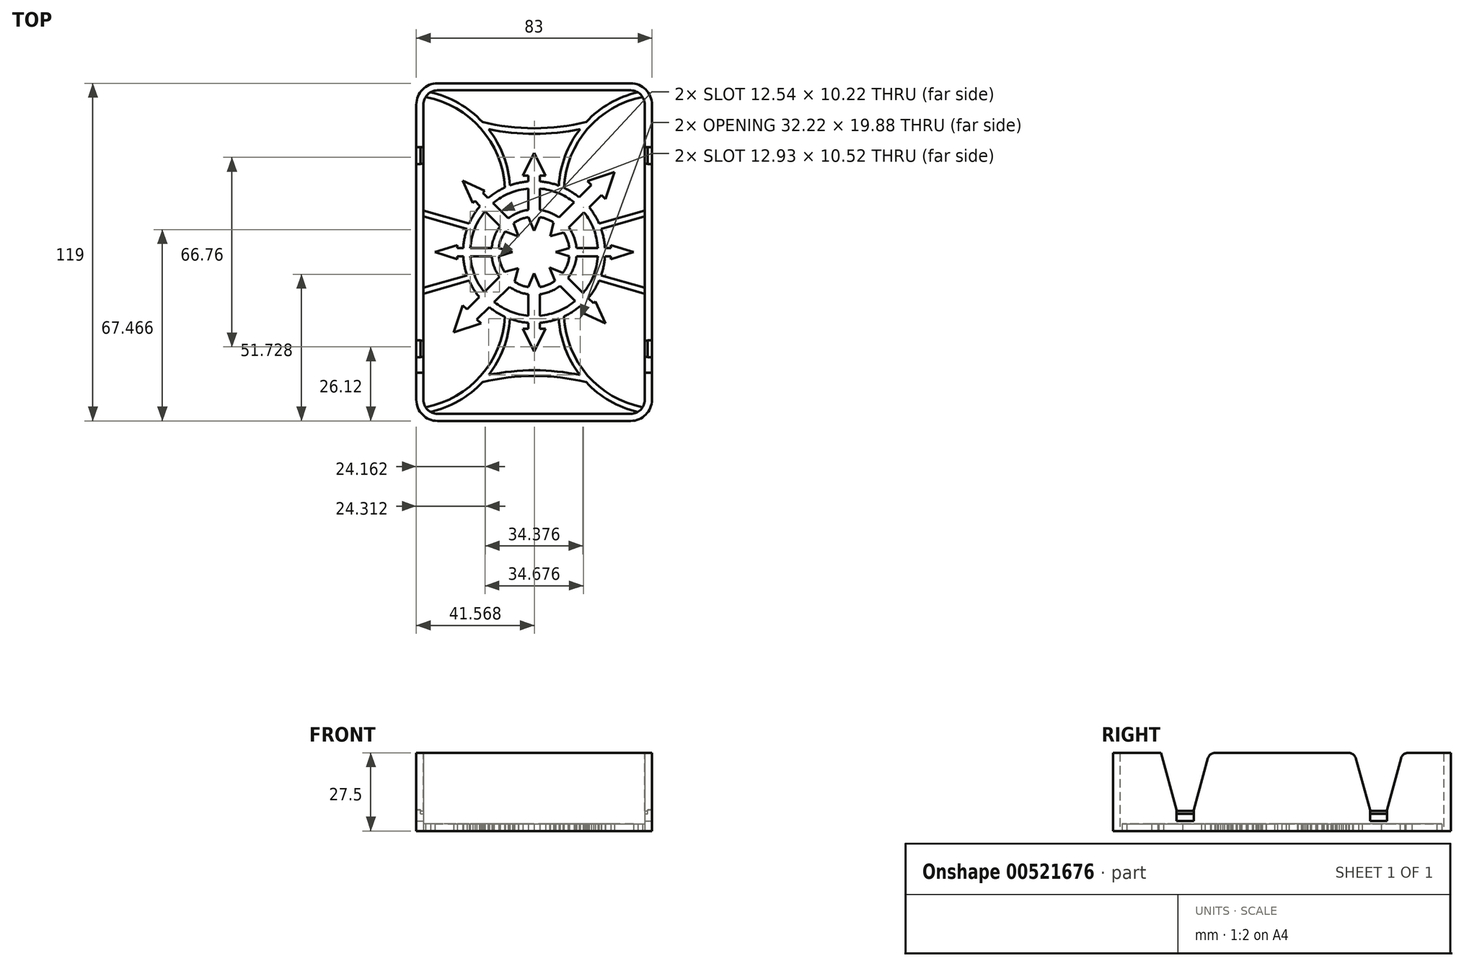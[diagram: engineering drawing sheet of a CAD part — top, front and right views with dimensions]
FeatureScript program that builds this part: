
annotation { "Feature Type Name" : "Feature", "Feature Type Description" : "" }
export const myFeature = defineFeature(function(context is Context, id is Id, definition is map)
    precondition{}
    {
        {
            var Q0;
            Q0=qCreatedBy(makeId("Top.planeOp"),FACE);
            var sketch = newSketch(context, id + "F0", { "sketchPlane" : qUnion([Q0])});
            skLineSegment(sketch, "E0.bottom", {"start": v(-34, 57) * mm, "end": v(34, 57) * mm});
            skLineSegment(sketch, "E0.top", {"start": v(-34, -57) * mm, "end": v(34, -57) * mm});
            skLineSegment(sketch, "E0.left", {"start": v(-39, 52) * mm, "end": v(-39, 14.68) * mm});
            skLineSegment(sketch, "E0.right", {"start": v(39, 52) * mm, "end": v(39, 14.68) * mm});
            skPoint(sketch, "E1.visualSharp", {"position": v(-39, 57) * mm});
            skArc(sketch, "E1.filletArc", {"start": v(-34, 57) * mm, "mid": v(-37.54, 55.54) * mm, "end": v(-39, 52) * mm});
            skPoint(sketch, "E2.visualSharp", {"position": v(39, 57) * mm});
            skArc(sketch, "E2.filletArc", {"start": v(39, 52) * mm, "mid": v(37.54, 55.54) * mm, "end": v(34, 57) * mm});
            skPoint(sketch, "E3.visualSharp", {"position": v(-39, -57) * mm});
            skArc(sketch, "E3.filletArc", {"start": v(-39, -52) * mm, "mid": v(-37.54, -55.54) * mm, "end": v(-34, -57) * mm});
            skPoint(sketch, "E4.visualSharp", {"position": v(39, -57) * mm});
            skArc(sketch, "E4.filletArc", {"start": v(34, -57) * mm, "mid": v(37.54, -55.54) * mm, "end": v(39, -52) * mm});
            skArc(sketch, "E5", {"start": v(-6.9, -10.43) * mm, "mid": v(-4.55, -11.64) * mm, "end": v(-2, -12.34) * mm});
            skArc(sketch, "E6.0", {"start": v(-8.7, -12.23) * mm, "mid": v(-5.5, -13.95) * mm, "end": v(-2, -14.87) * mm});
            skArc(sketch, "E7.0", {"start": v(-14.04, -17.58) * mm, "mid": v(-8.38, -20.88) * mm, "end": v(-2, -22.41) * mm});
            skArc(sketch, "E8.0", {"start": v(-15.82, -19.36) * mm, "mid": v(-13.18, -21.24) * mm, "end": v(-10.31, -22.77) * mm});
            skLineSegment(sketch, "E9", {"start": v(-20.15, -23.69) * mm, "end": v(-18.74, -25.1) * mm});
            skLineSegment(sketch, "E10", {"start": v(-23.69, -20.15) * mm, "end": v(-25.1, -18.74) * mm});
            skLineSegment(sketch, "E11", {"start": v(-28.28, -28.28) * mm, "end": v(-25.1, -18.74) * mm});
            skLineSegment(sketch, "E12", {"start": v(-28.28, -28.28) * mm, "end": v(-18.74, -25.1) * mm});
            skLineSegment(sketch, "E13.trimOffspring", {"start": v(-19.36, -15.82) * mm, "end": v(-23.69, -20.15) * mm});
            skLineSegment(sketch, "E14.trimOffspring", {"start": v(-15.82, -19.36) * mm, "end": v(-20.15, -23.69) * mm});
            skLineSegment(sketch, "E15", {"start": v(-6.9, -10.43) * mm, "end": v(-5.66, -5.66) * mm});
            skLineSegment(sketch, "E16", {"start": v(-5.66, -5.66) * mm, "end": v(-10.43, -6.9) * mm});
            skLineSegment(sketch, "E17.trimOffspring", {"start": v(-12.23, -8.7) * mm, "end": v(-17.58, -14.04) * mm});
            skLineSegment(sketch, "E18.trimOffspring", {"start": v(-8.7, -12.23) * mm, "end": v(-14.04, -17.58) * mm});
            skLineSegment(sketch, "E19.0", {"start": v(18.06, -20.89) * mm, "end": v(17.35, -21.6) * mm});
            skLineSegment(sketch, "E20.MirrorCS", {"start": v(20.89, -18.06) * mm, "end": v(21.6, -17.35) * mm});
            skLineSegment(sketch, "E21", {"start": v(25.13, -25.13) * mm, "end": v(17.35, -21.6) * mm});
            skLineSegment(sketch, "E22", {"start": v(25.13, -25.13) * mm, "end": v(21.6, -17.35) * mm});
            skArc(sketch, "E23.trimOffspring", {"start": v(19.04, -16.2) * mm, "mid": v(21.2, -13.26) * mm, "end": v(22.9, -10.03) * mm});
            skArc(sketch, "E24.trimOffspring", {"start": v(17.26, -14.43) * mm, "mid": v(20.88, -8.38) * mm, "end": v(22.45, -1.5) * mm});
            skLineSegment(sketch, "E25", {"start": v(7.31, -10.14) * mm, "end": v(5.47, -5.47) * mm});
            skLineSegment(sketch, "E26", {"start": v(5.47, -5.47) * mm, "end": v(10.14, -7.31) * mm});
            skArc(sketch, "E27.trimOffspring", {"start": v(11.93, -9.1) * mm, "mid": v(13.95, -5.5) * mm, "end": v(14.92, -1.5) * mm});
            skLineSegment(sketch, "E28.trimOffspring", {"start": v(19.04, -16.2) * mm, "end": v(20.89, -18.06) * mm});
            skLineSegment(sketch, "E29.trimOffspring", {"start": v(16.2, -19.04) * mm, "end": v(18.06, -20.89) * mm});
            skArc(sketch, "E30.trimOffspring", {"start": v(10.14, -7.31) * mm, "mid": v(11.64, -4.55) * mm, "end": v(12.4, -1.5) * mm});
            skLineSegment(sketch, "E31.trimOffspring", {"start": v(9.1, -11.93) * mm, "end": v(14.43, -17.26) * mm});
            skLineSegment(sketch, "E32.trimOffspring", {"start": v(11.93, -9.1) * mm, "end": v(17.26, -14.43) * mm});
            skLineSegment(sketch, "E33.MirrorCS", {"start": v(-11.93, 9.1) * mm, "end": v(-17.26, 14.43) * mm});
            skLineSegment(sketch, "E34.MirrorCS", {"start": v(-9.1, 11.93) * mm, "end": v(-14.43, 17.26) * mm});
            skLineSegment(sketch, "E35.MirrorCS", {"start": v(-5.47, 5.47) * mm, "end": v(-7.31, 10.14) * mm});
            skLineSegment(sketch, "E36.MirrorCS", {"start": v(-10.14, 7.31) * mm, "end": v(-5.47, 5.47) * mm});
            skLineSegment(sketch, "E37.MirrorCS", {"start": v(-16.2, 19.04) * mm, "end": v(-18.06, 20.89) * mm});
            skLineSegment(sketch, "E38.MirrorCS", {"start": v(-19.04, 16.2) * mm, "end": v(-20.89, 18.06) * mm});
            skLineSegment(sketch, "E39.MirrorCS", {"start": v(-20.89, 18.06) * mm, "end": v(-21.6, 17.35) * mm});
            skLineSegment(sketch, "E40.MirrorCS", {"start": v(-25.13, 25.13) * mm, "end": v(-21.6, 17.35) * mm});
            skLineSegment(sketch, "E41.MirrorCS", {"start": v(-25.13, 25.13) * mm, "end": v(-17.35, 21.6) * mm});
            skLineSegment(sketch, "E42.MirrorCS", {"start": v(-18.06, 20.89) * mm, "end": v(-17.35, 21.6) * mm});
            skArc(sketch, "E43.trimOffspring", {"start": v(-19.04, 16.2) * mm, "mid": v(-21.2, 13.26) * mm, "end": v(-22.9, 10.03) * mm});
            skArc(sketch, "E44.trimOffspring", {"start": v(-17.26, 14.43) * mm, "mid": v(-20.88, 8.38) * mm, "end": v(-22.45, 1.5) * mm});
            skArc(sketch, "E45.trimOffspring", {"start": v(-11.93, 9.1) * mm, "mid": v(-13.95, 5.5) * mm, "end": v(-14.92, 1.5) * mm});
            skArc(sketch, "E46.trimOffspring", {"start": v(-10.14, 7.31) * mm, "mid": v(-11.64, 4.55) * mm, "end": v(-12.4, 1.5) * mm});
            skLineSegment(sketch, "E47.0", {"start": v(-2, -27) * mm, "end": v(-4, -27) * mm});
            skLineSegment(sketch, "E48", {"start": v(0, -35) * mm, "end": v(-4, -27) * mm});
            skLineSegment(sketch, "E49.MirrorCS", {"start": v(2, -27) * mm, "end": v(4, -27) * mm});
            skLineSegment(sketch, "E50.MirrorCS", {"start": v(0, -35) * mm, "end": v(4, -27) * mm});
            skLineSegment(sketch, "E51", {"start": v(-2, -12.34) * mm, "end": v(0, -7.51) * mm});
            skLineSegment(sketch, "E52", {"start": v(0, -7.51) * mm, "end": v(2, -12.34) * mm});
            skArc(sketch, "E53.trimOffspring", {"start": v(2, -12.34) * mm, "mid": v(4.78, -11.55) * mm, "end": v(7.31, -10.14) * mm});
            skArc(sketch, "E54.trimOffspring", {"start": v(2, -14.87) * mm, "mid": v(5.74, -13.86) * mm, "end": v(9.1, -11.93) * mm});
            skArc(sketch, "E55.trimOffspring", {"start": v(2, -22.41) * mm, "mid": v(8.61, -20.79) * mm, "end": v(14.43, -17.26) * mm});
            skArc(sketch, "E56.trimOffspring", {"start": v(2, -24.92) * mm, "mid": v(5.4, -24.41) * mm, "end": v(8.7, -23.44) * mm});
            skLineSegment(sketch, "E57.trimOffspring", {"start": v(-2, -24.92) * mm, "end": v(-2, -27) * mm});
            skLineSegment(sketch, "E58.trimOffspring", {"start": v(2, -24.92) * mm, "end": v(2, -27) * mm});
            skLineSegment(sketch, "E59.trimOffspring", {"start": v(2, -14.87) * mm, "end": v(2, -22.41) * mm});
            skLineSegment(sketch, "E60.trimOffspring", {"start": v(-2, -14.87) * mm, "end": v(-2, -22.41) * mm});
            skLineSegment(sketch, "E61.MirrorCS", {"start": v(-2, 12.34) * mm, "end": v(0, 7.51) * mm});
            skLineSegment(sketch, "E62.MirrorCS", {"start": v(0, 7.51) * mm, "end": v(2, 12.34) * mm});
            skLineSegment(sketch, "E63.MirrorCS", {"start": v(-2, 14.87) * mm, "end": v(-2, 22.41) * mm});
            skLineSegment(sketch, "E64.MirrorCS", {"start": v(2, 14.87) * mm, "end": v(2, 22.41) * mm});
            skLineSegment(sketch, "E65.MirrorCS", {"start": v(0, 35) * mm, "end": v(-4, 27) * mm});
            skLineSegment(sketch, "E66.MirrorCS", {"start": v(0, 35) * mm, "end": v(4, 27) * mm});
            skLineSegment(sketch, "E67.MirrorCS", {"start": v(2, 27) * mm, "end": v(4, 27) * mm});
            skLineSegment(sketch, "E68.MirrorCS", {"start": v(2, 24.92) * mm, "end": v(2, 27) * mm});
            skLineSegment(sketch, "E69.MirrorCS", {"start": v(-2, 24.92) * mm, "end": v(-2, 27) * mm});
            skLineSegment(sketch, "E70.MirrorCS", {"start": v(-2, 27) * mm, "end": v(-4, 27) * mm});
            skArc(sketch, "E71.trimOffspring", {"start": v(-2, 24.92) * mm, "mid": v(-5.32, 24.43) * mm, "end": v(-8.54, 23.5) * mm});
            skArc(sketch, "E72.trimOffspring", {"start": v(-2, 22.41) * mm, "mid": v(-8.61, 20.79) * mm, "end": v(-14.43, 17.26) * mm});
            skArc(sketch, "E73.trimOffspring", {"start": v(-2, 14.87) * mm, "mid": v(-5.74, 13.86) * mm, "end": v(-9.1, 11.93) * mm});
            skArc(sketch, "E74.trimOffspring", {"start": v(-2, 12.34) * mm, "mid": v(-4.78, 11.55) * mm, "end": v(-7.31, 10.14) * mm});
            skLineSegment(sketch, "E75.MirrorCS", {"start": v(5.66, 5.66) * mm, "end": v(6.9, 10.43) * mm});
            skLineSegment(sketch, "E76.MirrorCS", {"start": v(10.43, 6.9) * mm, "end": v(5.66, 5.66) * mm});
            skLineSegment(sketch, "E77.MirrorCS", {"start": v(8.7, 12.23) * mm, "end": v(14.04, 17.58) * mm});
            skLineSegment(sketch, "E78.MirrorCS", {"start": v(12.23, 8.7) * mm, "end": v(17.58, 14.04) * mm});
            skLineSegment(sketch, "E79.MirrorCS", {"start": v(19.36, 15.82) * mm, "end": v(23.69, 20.15) * mm});
            skLineSegment(sketch, "E80.MirrorCS", {"start": v(23.69, 20.15) * mm, "end": v(25.1, 18.74) * mm});
            skLineSegment(sketch, "E81.MirrorCS", {"start": v(28.28, 28.28) * mm, "end": v(25.1, 18.74) * mm});
            skLineSegment(sketch, "E82.MirrorCS", {"start": v(28.28, 28.28) * mm, "end": v(18.74, 25.1) * mm});
            skLineSegment(sketch, "E83.MirrorCS", {"start": v(20.15, 23.69) * mm, "end": v(18.74, 25.1) * mm});
            skLineSegment(sketch, "E84.MirrorCS", {"start": v(15.82, 19.36) * mm, "end": v(20.15, 23.69) * mm});
            skArc(sketch, "E85.trimOffspring", {"start": v(6.9, 10.43) * mm, "mid": v(4.55, 11.64) * mm, "end": v(2, 12.34) * mm});
            skArc(sketch, "E86.trimOffspring", {"start": v(8.7, 12.23) * mm, "mid": v(5.5, 13.95) * mm, "end": v(2, 14.87) * mm});
            skArc(sketch, "E87.trimOffspring", {"start": v(14.04, 17.58) * mm, "mid": v(8.38, 20.88) * mm, "end": v(2, 22.41) * mm});
            skArc(sketch, "E88.trimOffspring", {"start": v(15.82, 19.36) * mm, "mid": v(13.29, 21.18) * mm, "end": v(10.55, 22.67) * mm});
            skLineSegment(sketch, "E89.0", {"start": v(-14.92, 1.5) * mm, "end": v(-22.45, 1.5) * mm});
            skLineSegment(sketch, "E90.0", {"start": v(-14.92, -1.5) * mm, "end": v(-22.45, -1.5) * mm});
            skLineSegment(sketch, "E91.0", {"start": v(-27, 1.5) * mm, "end": v(-27, 2.5) * mm});
            skLineSegment(sketch, "E92", {"start": v(-35, 0) * mm, "end": v(-27, 2.5) * mm});
            skLineSegment(sketch, "E93.MirrorCS", {"start": v(-35, 0) * mm, "end": v(-27, -2.5) * mm});
            skLineSegment(sketch, "E94.MirrorCS", {"start": v(-27, -1.5) * mm, "end": v(-27, -2.5) * mm});
            skLineSegment(sketch, "E95", {"start": v(-12.4, 1.5) * mm, "end": v(-7.65, 0) * mm});
            skLineSegment(sketch, "E96", {"start": v(-7.65, 0) * mm, "end": v(-12.4, -1.5) * mm});
            skArc(sketch, "E97.trimOffspring", {"start": v(-24.95, -1.5) * mm, "mid": v(-24.52, -4.88) * mm, "end": v(-23.63, -8.16) * mm});
            skArc(sketch, "E98.trimOffspring", {"start": v(-12.4, -1.5) * mm, "mid": v(-11.73, -4.31) * mm, "end": v(-10.43, -6.9) * mm});
            skArc(sketch, "E99.trimOffspring", {"start": v(-14.92, -1.5) * mm, "mid": v(-14.04, -5.27) * mm, "end": v(-12.23, -8.7) * mm});
            skArc(sketch, "E100.trimOffspring", {"start": v(-22.45, -1.5) * mm, "mid": v(-20.97, -8.14) * mm, "end": v(-17.58, -14.04) * mm});
            skLineSegment(sketch, "E101.MirrorCS", {"start": v(7.65, 0) * mm, "end": v(12.4, -1.5) * mm});
            skLineSegment(sketch, "E102.MirrorCS", {"start": v(12.4, 1.5) * mm, "end": v(7.65, 0) * mm});
            skLineSegment(sketch, "E103.MirrorCS", {"start": v(14.92, 1.5) * mm, "end": v(22.45, 1.5) * mm});
            skLineSegment(sketch, "E104.MirrorCS", {"start": v(14.92, -1.5) * mm, "end": v(22.45, -1.5) * mm});
            skLineSegment(sketch, "E105.MirrorCS", {"start": v(27, 1.5) * mm, "end": v(27, 2.5) * mm});
            skLineSegment(sketch, "E106.MirrorCS", {"start": v(27, -1.5) * mm, "end": v(27, -2.5) * mm});
            skLineSegment(sketch, "E107.MirrorCS", {"start": v(35, 0) * mm, "end": v(27, -2.5) * mm});
            skLineSegment(sketch, "E108.MirrorCS", {"start": v(35, 0) * mm, "end": v(27, 2.5) * mm});
            skLineSegment(sketch, "E109.trimOffspring", {"start": v(-24.95, 1.5) * mm, "end": v(-27, 1.5) * mm});
            skLineSegment(sketch, "E110.trimOffspring", {"start": v(-24.95, -1.5) * mm, "end": v(-27, -1.5) * mm});
            skArc(sketch, "E111.trimOffspring", {"start": v(12.4, 1.5) * mm, "mid": v(11.73, 4.31) * mm, "end": v(10.43, 6.9) * mm});
            skArc(sketch, "E112.trimOffspring", {"start": v(14.92, 1.5) * mm, "mid": v(14.04, 5.27) * mm, "end": v(12.23, 8.7) * mm});
            skArc(sketch, "E113.trimOffspring", {"start": v(22.45, 1.5) * mm, "mid": v(20.97, 8.14) * mm, "end": v(17.58, 14.04) * mm});
            skArc(sketch, "E114.trimOffspring", {"start": v(24.95, 1.5) * mm, "mid": v(24.52, 4.88) * mm, "end": v(23.63, 8.16) * mm});
            skLineSegment(sketch, "E115.trimOffspring", {"start": v(24.95, 1.5) * mm, "end": v(27, 1.5) * mm});
            skLineSegment(sketch, "E116.trimOffspring", {"start": v(24.95, -1.5) * mm, "end": v(27, -1.5) * mm});
            skArc(sketch, "E117.0", {"start": v(-34, 59.5) * mm, "mid": v(-39.3, 57.3) * mm, "end": v(-41.5, 52) * mm});
            skLineSegment(sketch, "E117.1", {"start": v(-41.5, 52) * mm, "end": v(-41.5, -52) * mm});
            skLineSegment(sketch, "E117.2", {"start": v(-34, 59.5) * mm, "end": v(34, 59.5) * mm});
            skArc(sketch, "E117.3", {"start": v(-41.5, -52) * mm, "mid": v(-39.3, -57.3) * mm, "end": v(-34, -59.5) * mm});
            skArc(sketch, "E117.4", {"start": v(41.5, 52) * mm, "mid": v(39.3, 57.3) * mm, "end": v(34, 59.5) * mm});
            skLineSegment(sketch, "E117.5", {"start": v(41.5, 52) * mm, "end": v(41.5, -52) * mm});
            skArc(sketch, "E117.6", {"start": v(34, -59.5) * mm, "mid": v(39.3, -57.3) * mm, "end": v(41.5, -52) * mm});
            skLineSegment(sketch, "E117.7", {"start": v(-34, -59.5) * mm, "end": v(34, -59.5) * mm});
            skArc(sketch, "E118.0", {"start": v(-36.5, -56.33) * mm, "mid": v(-26.57, -52.47) * mm, "end": v(-18.22, -45.86) * mm});
            skArc(sketch, "E119.0", {"start": v(-38.24, -54.65) * mm, "mid": v(-18.75, -43.55) * mm, "end": v(-10.31, -22.77) * mm});
            skArc(sketch, "E120.0", {"start": v(8.7, -23.44) * mm, "mid": v(10.94, -33.94) * mm, "end": v(16.18, -43.32) * mm});
            skArc(sketch, "E121.0", {"start": v(10.55, -22.67) * mm, "mid": v(18.84, -43.47) * mm, "end": v(38.24, -54.66) * mm});
            skArc(sketch, "E122.MirrorCS", {"start": v(-36.5, 56.33) * mm, "mid": v(-26.57, 52.47) * mm, "end": v(-18.22, 45.86) * mm});
            skArc(sketch, "E123.MirrorCS", {"start": v(-38.24, 54.65) * mm, "mid": v(-18.75, 43.55) * mm, "end": v(-10.31, 22.77) * mm});
            skArc(sketch, "E124.MirrorCS", {"start": v(10.55, 22.67) * mm, "mid": v(18.84, 43.47) * mm, "end": v(38.24, 54.66) * mm});
            skArc(sketch, "E125.MirrorCS", {"start": v(8.7, 23.44) * mm, "mid": v(10.94, 33.94) * mm, "end": v(16.18, 43.32) * mm});
            skArc(sketch, "E126.0", {"start": v(16.18, -43.32) * mm, "mid": v(0.07, -41.65) * mm, "end": v(-16.04, -43.32) * mm});
            skArc(sketch, "E127.0", {"start": v(18.35, -45.86) * mm, "mid": v(0.06, -43.65) * mm, "end": v(-18.22, -45.86) * mm});
            skArc(sketch, "E128.MirrorCS", {"start": v(16.18, 43.32) * mm, "mid": v(0.07, 41.65) * mm, "end": v(-16.04, 43.32) * mm});
            skArc(sketch, "E129.MirrorCS", {"start": v(18.35, 45.86) * mm, "mid": v(0.06, 43.65) * mm, "end": v(-18.22, 45.86) * mm});
            skArc(sketch, "E130.trimOffspring", {"start": v(-16.04, -43.32) * mm, "mid": v(-10.8, -33.97) * mm, "end": v(-8.54, -23.5) * mm});
            skArc(sketch, "E131.trimOffspring", {"start": v(18.35, -45.86) * mm, "mid": v(26.64, -52.45) * mm, "end": v(36.5, -56.33) * mm});
            skArc(sketch, "E132.trimOffspring", {"start": v(10.55, -22.67) * mm, "mid": v(13.5, -21.04) * mm, "end": v(16.2, -19.04) * mm});
            skArc(sketch, "E133.trimOffspring", {"start": v(-8.54, -23.5) * mm, "mid": v(-5.32, -24.43) * mm, "end": v(-2, -24.92) * mm});
            skArc(sketch, "E134.trimOffspring", {"start": v(-10.31, 22.77) * mm, "mid": v(-13.4, 21.11) * mm, "end": v(-16.2, 19.04) * mm});
            skArc(sketch, "E135.trimOffspring", {"start": v(8.7, 23.44) * mm, "mid": v(5.4, 24.41) * mm, "end": v(2, 24.92) * mm});
            skArc(sketch, "E136.trimOffspring", {"start": v(18.35, 45.86) * mm, "mid": v(26.64, 52.45) * mm, "end": v(36.5, 56.33) * mm});
            skArc(sketch, "E137.trimOffspring", {"start": v(-16.04, 43.32) * mm, "mid": v(-10.8, 33.97) * mm, "end": v(-8.54, 23.5) * mm});
            skLineSegment(sketch, "E138.0", {"start": v(-23.63, -8.16) * mm, "end": v(-39, -12.6) * mm});
            skLineSegment(sketch, "E139.0", {"start": v(-22.9, -10.03) * mm, "end": v(-39, -14.68) * mm});
            skLineSegment(sketch, "E140.trimOffspring", {"start": v(-39, -14.68) * mm, "end": v(-39, -52) * mm});
            skArc(sketch, "E141.trimOffspring", {"start": v(-22.9, -10.03) * mm, "mid": v(-21.33, -13.05) * mm, "end": v(-19.36, -15.82) * mm});
            skLineSegment(sketch, "E142.MirrorCS", {"start": v(-23.63, 8.16) * mm, "end": v(-39, 12.6) * mm});
            skLineSegment(sketch, "E143.MirrorCS", {"start": v(-22.9, 10.03) * mm, "end": v(-39, 14.68) * mm});
            skLineSegment(sketch, "E144.MirrorCS", {"start": v(23.63, -8.16) * mm, "end": v(39, -12.6) * mm});
            skLineSegment(sketch, "E145.MirrorCS", {"start": v(22.9, -10.03) * mm, "end": v(39, -14.68) * mm});
            skLineSegment(sketch, "E146.MirrorCS", {"start": v(23.63, 8.16) * mm, "end": v(39, 12.6) * mm});
            skLineSegment(sketch, "E147.MirrorCS", {"start": v(22.9, 10.03) * mm, "end": v(39, 14.68) * mm});
            skLineSegment(sketch, "E148.trimOffspring", {"start": v(-39, 12.6) * mm, "end": v(-39, -12.6) * mm});
            skArc(sketch, "E149.trimOffspring", {"start": v(-23.63, 8.16) * mm, "mid": v(-24.52, 4.88) * mm, "end": v(-24.95, 1.5) * mm});
            skArc(sketch, "E150.trimOffspring", {"start": v(22.9, 10.03) * mm, "mid": v(21.33, 13.05) * mm, "end": v(19.36, 15.82) * mm});
            skLineSegment(sketch, "E151.trimOffspring", {"start": v(39, 12.6) * mm, "end": v(39, -12.6) * mm});
            skArc(sketch, "E152.trimOffspring", {"start": v(23.63, -8.16) * mm, "mid": v(24.52, -4.88) * mm, "end": v(24.95, -1.5) * mm});
            skLineSegment(sketch, "E153.trimOffspring", {"start": v(39, -14.68) * mm, "end": v(39, -52) * mm});
            skSolve(sketch);
        }
        {
            var Q0;
            Q0 = qSketchRegion(id + "F0", true);
            extrude(context, id + "F1", {"entities" : qUnion([Q0]), "depth" : 2.5 * mm, "offsetDistance" : 25 * mm});
        }
        {
            var Q0;
            Q0=makeQuery(id+"F1.opExtrude","CAP_FACE",FACE,{"disambiguationData":[OSD([sQuery(id+"F0.wireOp",EDGE,"E0.bottom"),sQuery(id+"F0.wireOp",EDGE,"E0.top"),sQuery(id+"F0.wireOp",EDGE,"E0.left"),sQuery(id+"F0.wireOp",EDGE,"E0.right"),sQuery(id+"F0.wireOp",EDGE,"E1.filletArc"),sQuery(id+"F0.wireOp",EDGE,"E2.filletArc"),sQuery(id+"F0.wireOp",EDGE,"E3.filletArc"),sQuery(id+"F0.wireOp",EDGE,"E4.filletArc"),sQuery(id+"F0.wireOp",EDGE,"E5"),sQuery(id+"F0.wireOp",EDGE,"E6.0"),sQuery(id+"F0.wireOp",EDGE,"E7.0"),sQuery(id+"F0.wireOp",EDGE,"E8.0"),sQuery(id+"F0.wireOp",EDGE,"E9"),sQuery(id+"F0.wireOp",EDGE,"E10"),sQuery(id+"F0.wireOp",EDGE,"E11"),sQuery(id+"F0.wireOp",EDGE,"E12"),sQuery(id+"F0.wireOp",EDGE,"E13.trimOffspring"),sQuery(id+"F0.wireOp",EDGE,"E14.trimOffspring"),sQuery(id+"F0.wireOp",EDGE,"E15"),sQuery(id+"F0.wireOp",EDGE,"E16"),sQuery(id+"F0.wireOp",EDGE,"E17.trimOffspring"),sQuery(id+"F0.wireOp",EDGE,"E18.trimOffspring"),sQuery(id+"F0.wireOp",EDGE,"E19.0"),sQuery(id+"F0.wireOp",EDGE,"E20.MirrorCS"),sQuery(id+"F0.wireOp",EDGE,"E21"),sQuery(id+"F0.wireOp",EDGE,"E22"),sQuery(id+"F0.wireOp",EDGE,"E23.trimOffspring"),sQuery(id+"F0.wireOp",EDGE,"E24.trimOffspring"),sQuery(id+"F0.wireOp",EDGE,"E25"),sQuery(id+"F0.wireOp",EDGE,"E26"),sQuery(id+"F0.wireOp",EDGE,"E27.trimOffspring"),sQuery(id+"F0.wireOp",EDGE,"E28.trimOffspring"),sQuery(id+"F0.wireOp",EDGE,"E29.trimOffspring"),sQuery(id+"F0.wireOp",EDGE,"E30.trimOffspring"),sQuery(id+"F0.wireOp",EDGE,"E31.trimOffspring"),sQuery(id+"F0.wireOp",EDGE,"E32.trimOffspring"),sQuery(id+"F0.wireOp",EDGE,"E33.MirrorCS"),sQuery(id+"F0.wireOp",EDGE,"E34.MirrorCS"),sQuery(id+"F0.wireOp",EDGE,"E35.MirrorCS"),sQuery(id+"F0.wireOp",EDGE,"E36.MirrorCS"),sQuery(id+"F0.wireOp",EDGE,"E37.MirrorCS"),sQuery(id+"F0.wireOp",EDGE,"E38.MirrorCS"),sQuery(id+"F0.wireOp",EDGE,"E39.MirrorCS"),sQuery(id+"F0.wireOp",EDGE,"E40.MirrorCS"),sQuery(id+"F0.wireOp",EDGE,"E41.MirrorCS"),sQuery(id+"F0.wireOp",EDGE,"E42.MirrorCS"),sQuery(id+"F0.wireOp",EDGE,"E43.trimOffspring"),sQuery(id+"F0.wireOp",EDGE,"E44.trimOffspring"),sQuery(id+"F0.wireOp",EDGE,"E45.trimOffspring"),sQuery(id+"F0.wireOp",EDGE,"E46.trimOffspring"),sQuery(id+"F0.wireOp",EDGE,"E47.0"),sQuery(id+"F0.wireOp",EDGE,"E48"),sQuery(id+"F0.wireOp",EDGE,"E49.MirrorCS"),sQuery(id+"F0.wireOp",EDGE,"E50.MirrorCS"),sQuery(id+"F0.wireOp",EDGE,"E51"),sQuery(id+"F0.wireOp",EDGE,"E52"),sQuery(id+"F0.wireOp",EDGE,"E53.trimOffspring"),sQuery(id+"F0.wireOp",EDGE,"E54.trimOffspring"),sQuery(id+"F0.wireOp",EDGE,"E55.trimOffspring"),sQuery(id+"F0.wireOp",EDGE,"E56.trimOffspring"),sQuery(id+"F0.wireOp",EDGE,"E57.trimOffspring"),sQuery(id+"F0.wireOp",EDGE,"E58.trimOffspring"),sQuery(id+"F0.wireOp",EDGE,"E59.trimOffspring"),sQuery(id+"F0.wireOp",EDGE,"E60.trimOffspring"),sQuery(id+"F0.wireOp",EDGE,"E61.MirrorCS"),sQuery(id+"F0.wireOp",EDGE,"E62.MirrorCS"),sQuery(id+"F0.wireOp",EDGE,"E63.MirrorCS"),sQuery(id+"F0.wireOp",EDGE,"E64.MirrorCS"),sQuery(id+"F0.wireOp",EDGE,"E65.MirrorCS"),sQuery(id+"F0.wireOp",EDGE,"E66.MirrorCS"),sQuery(id+"F0.wireOp",EDGE,"E67.MirrorCS"),sQuery(id+"F0.wireOp",EDGE,"E68.MirrorCS"),sQuery(id+"F0.wireOp",EDGE,"E69.MirrorCS"),sQuery(id+"F0.wireOp",EDGE,"E70.MirrorCS"),sQuery(id+"F0.wireOp",EDGE,"E71.trimOffspring"),sQuery(id+"F0.wireOp",EDGE,"E72.trimOffspring"),sQuery(id+"F0.wireOp",EDGE,"E73.trimOffspring"),sQuery(id+"F0.wireOp",EDGE,"E74.trimOffspring"),sQuery(id+"F0.wireOp",EDGE,"E75.MirrorCS"),sQuery(id+"F0.wireOp",EDGE,"E76.MirrorCS"),sQuery(id+"F0.wireOp",EDGE,"E77.MirrorCS"),sQuery(id+"F0.wireOp",EDGE,"E78.MirrorCS"),sQuery(id+"F0.wireOp",EDGE,"E79.MirrorCS"),sQuery(id+"F0.wireOp",EDGE,"E80.MirrorCS"),sQuery(id+"F0.wireOp",EDGE,"E81.MirrorCS"),sQuery(id+"F0.wireOp",EDGE,"E82.MirrorCS"),sQuery(id+"F0.wireOp",EDGE,"E83.MirrorCS"),sQuery(id+"F0.wireOp",EDGE,"E84.MirrorCS"),sQuery(id+"F0.wireOp",EDGE,"E85.trimOffspring"),sQuery(id+"F0.wireOp",EDGE,"E86.trimOffspring"),sQuery(id+"F0.wireOp",EDGE,"E87.trimOffspring"),sQuery(id+"F0.wireOp",EDGE,"E88.trimOffspring"),sQuery(id+"F0.wireOp",EDGE,"E89.0"),sQuery(id+"F0.wireOp",EDGE,"E90.0"),sQuery(id+"F0.wireOp",EDGE,"E91.0"),sQuery(id+"F0.wireOp",EDGE,"E92"),sQuery(id+"F0.wireOp",EDGE,"E93.MirrorCS"),sQuery(id+"F0.wireOp",EDGE,"E94.MirrorCS"),sQuery(id+"F0.wireOp",EDGE,"E95"),sQuery(id+"F0.wireOp",EDGE,"E96"),sQuery(id+"F0.wireOp",EDGE,"E97.trimOffspring"),sQuery(id+"F0.wireOp",EDGE,"E98.trimOffspring"),sQuery(id+"F0.wireOp",EDGE,"E99.trimOffspring"),sQuery(id+"F0.wireOp",EDGE,"E100.trimOffspring"),sQuery(id+"F0.wireOp",EDGE,"E101.MirrorCS"),sQuery(id+"F0.wireOp",EDGE,"E102.MirrorCS"),sQuery(id+"F0.wireOp",EDGE,"E103.MirrorCS"),sQuery(id+"F0.wireOp",EDGE,"E104.MirrorCS"),sQuery(id+"F0.wireOp",EDGE,"E105.MirrorCS"),sQuery(id+"F0.wireOp",EDGE,"E106.MirrorCS"),sQuery(id+"F0.wireOp",EDGE,"E107.MirrorCS"),sQuery(id+"F0.wireOp",EDGE,"E108.MirrorCS"),sQuery(id+"F0.wireOp",EDGE,"E109.trimOffspring"),sQuery(id+"F0.wireOp",EDGE,"E110.trimOffspring"),sQuery(id+"F0.wireOp",EDGE,"E111.trimOffspring"),sQuery(id+"F0.wireOp",EDGE,"E112.trimOffspring"),sQuery(id+"F0.wireOp",EDGE,"E113.trimOffspring"),sQuery(id+"F0.wireOp",EDGE,"E114.trimOffspring"),sQuery(id+"F0.wireOp",EDGE,"E115.trimOffspring"),sQuery(id+"F0.wireOp",EDGE,"E116.trimOffspring"),sQuery(id+"F0.wireOp",EDGE,"E117.0"),sQuery(id+"F0.wireOp",EDGE,"E117.1"),sQuery(id+"F0.wireOp",EDGE,"E117.2"),sQuery(id+"F0.wireOp",EDGE,"E117.3"),sQuery(id+"F0.wireOp",EDGE,"E117.4"),sQuery(id+"F0.wireOp",EDGE,"E117.5"),sQuery(id+"F0.wireOp",EDGE,"E117.6"),sQuery(id+"F0.wireOp",EDGE,"E117.7"),sQuery(id+"F0.wireOp",EDGE,"E118.0"),sQuery(id+"F0.wireOp",EDGE,"E119.0"),sQuery(id+"F0.wireOp",EDGE,"E120.0"),sQuery(id+"F0.wireOp",EDGE,"E121.0"),sQuery(id+"F0.wireOp",EDGE,"E122.MirrorCS"),sQuery(id+"F0.wireOp",EDGE,"E123.MirrorCS"),sQuery(id+"F0.wireOp",EDGE,"E124.MirrorCS"),sQuery(id+"F0.wireOp",EDGE,"E125.MirrorCS"),sQuery(id+"F0.wireOp",EDGE,"E126.0"),sQuery(id+"F0.wireOp",EDGE,"E127.0"),sQuery(id+"F0.wireOp",EDGE,"E128.MirrorCS"),sQuery(id+"F0.wireOp",EDGE,"E129.MirrorCS"),sQuery(id+"F0.wireOp",EDGE,"E130.trimOffspring"),sQuery(id+"F0.wireOp",EDGE,"E131.trimOffspring"),sQuery(id+"F0.wireOp",EDGE,"E132.trimOffspring"),sQuery(id+"F0.wireOp",EDGE,"E133.trimOffspring"),sQuery(id+"F0.wireOp",EDGE,"E134.trimOffspring"),sQuery(id+"F0.wireOp",EDGE,"E135.trimOffspring"),sQuery(id+"F0.wireOp",EDGE,"E136.trimOffspring"),sQuery(id+"F0.wireOp",EDGE,"E137.trimOffspring"),sQuery(id+"F0.wireOp",EDGE,"E138.0"),sQuery(id+"F0.wireOp",EDGE,"E139.0"),sQuery(id+"F0.wireOp",EDGE,"E140.trimOffspring"),sQuery(id+"F0.wireOp",EDGE,"E141.trimOffspring"),sQuery(id+"F0.wireOp",EDGE,"E142.MirrorCS"),sQuery(id+"F0.wireOp",EDGE,"E143.MirrorCS"),sQuery(id+"F0.wireOp",EDGE,"E144.MirrorCS"),sQuery(id+"F0.wireOp",EDGE,"E145.MirrorCS"),sQuery(id+"F0.wireOp",EDGE,"E146.MirrorCS"),sQuery(id+"F0.wireOp",EDGE,"E147.MirrorCS"),sQuery(id+"F0.wireOp",EDGE,"E148.trimOffspring"),sQuery(id+"F0.wireOp",EDGE,"E149.trimOffspring"),sQuery(id+"F0.wireOp",EDGE,"E150.trimOffspring"),sQuery(id+"F0.wireOp",EDGE,"E151.trimOffspring"),sQuery(id+"F0.wireOp",EDGE,"E152.trimOffspring"),sQuery(id+"F0.wireOp",EDGE,"E153.trimOffspring")])],"isStart":false});
            var sketch = newSketch(context, id + "F2", { "sketchPlane" : qUnion([Q0])});
            skLineSegment(sketch, "E154.bottom", {"start": v(-34, 59.5) * mm, "end": v(34, 59.5) * mm});
            skLineSegment(sketch, "E154.top", {"start": v(-34, -59.5) * mm, "end": v(34, -59.5) * mm});
            skLineSegment(sketch, "E154.left", {"start": v(-41.5, 52) * mm, "end": v(-41.5, -52) * mm});
            skLineSegment(sketch, "E154.right", {"start": v(41.5, 52) * mm, "end": v(41.5, -52) * mm});
            skPoint(sketch, "E155.visualSharp", {"position": v(-41.5, 59.5) * mm});
            skArc(sketch, "E155.filletArc", {"start": v(-34, 59.5) * mm, "mid": v(-39.3, 57.3) * mm, "end": v(-41.5, 52) * mm});
            skPoint(sketch, "E156.visualSharp", {"position": v(41.5, 59.5) * mm});
            skArc(sketch, "E156.filletArc", {"start": v(41.5, 52) * mm, "mid": v(39.3, 57.3) * mm, "end": v(34, 59.5) * mm});
            skPoint(sketch, "E157.visualSharp", {"position": v(-41.5, -59.5) * mm});
            skArc(sketch, "E157.filletArc", {"start": v(-41.5, -52) * mm, "mid": v(-39.3, -57.3) * mm, "end": v(-34, -59.5) * mm});
            skPoint(sketch, "E158.visualSharp", {"position": v(41.5, -59.5) * mm});
            skArc(sketch, "E158.filletArc", {"start": v(34, -59.5) * mm, "mid": v(39.3, -57.3) * mm, "end": v(41.5, -52) * mm});
            skArc(sketch, "E159.0", {"start": v(-34, 57) * mm, "mid": v(-37.54, 55.54) * mm, "end": v(-39, 52) * mm});
            skLineSegment(sketch, "E159.1", {"start": v(-39, 52) * mm, "end": v(-39, -52) * mm});
            skLineSegment(sketch, "E159.2", {"start": v(-34, 57) * mm, "end": v(34, 57) * mm});
            skArc(sketch, "E159.3", {"start": v(-39, -52) * mm, "mid": v(-37.54, -55.54) * mm, "end": v(-34, -57) * mm});
            skArc(sketch, "E159.4", {"start": v(39, 52) * mm, "mid": v(37.54, 55.54) * mm, "end": v(34, 57) * mm});
            skLineSegment(sketch, "E159.5", {"start": v(39, 52) * mm, "end": v(39, -52) * mm});
            skArc(sketch, "E159.6", {"start": v(34, -57) * mm, "mid": v(37.54, -55.54) * mm, "end": v(39, -52) * mm});
            skLineSegment(sketch, "E159.7", {"start": v(-34, -57) * mm, "end": v(34, -57) * mm});
            skSolve(sketch);
        }
        {
            var Q0;
            Q0 = qSketchRegion(id + "F2", true);
            extrude(context, id + "F3", {"entities" : qUnion([Q0]), "operationType" : NewBodyOperationType.ADD, "depth" : 25 * mm, "offsetDistance" : 25 * mm});
        }
        {
            var Q0;
            Q0=makeQuery(id+"F3.boolean.opBoolean","MERGE",FACE,{"derivedFrom":[makeQuery(id+"F1.opExtrude","SWEPT_FACE",FACE,{"disambiguationData":[OSD([sQuery(id+"F0.wireOp",EDGE,"E117.5")])]}),makeQuery(id+"F3.opExtrude","SWEPT_FACE",FACE,{"disambiguationData":[OSD([sQuery(id+"F2.wireOp",EDGE,"E154.right")])]})]});
            var sketch = newSketch(context, id + "F4", { "sketchPlane" : qUnion([Q0])});
            skLineSegment(sketch, "E160", {"start": v(0, 27.5) * mm, "end": v(0, 0) * mm});
            skLineSegment(sketch, "E161.0", {"start": v(-31.17, 7) * mm, "end": v(-25.48, 27.5) * mm});
            skLineSegment(sketch, "E161.1", {"start": v(-36.93, 7) * mm, "end": v(-31.17, 7) * mm});
            skLineSegment(sketch, "E161.2", {"start": v(-42.52, 27.5) * mm, "end": v(-36.93, 7) * mm});
            skLineSegment(sketch, "E162.0", {"start": v(-37.05, 6) * mm, "end": v(-37.05, 3.5) * mm});
            skLineSegment(sketch, "E163.0", {"start": v(-37.05, 6) * mm, "end": v(-31.05, 6) * mm});
            skLineSegment(sketch, "E164.0", {"start": v(-31.05, 6) * mm, "end": v(-31.05, 3.5) * mm});
            skLineSegment(sketch, "E165.0", {"start": v(-37.05, 3.5) * mm, "end": v(-31.05, 3.5) * mm});
            skLineSegment(sketch, "E166", {"start": v(-42.52, 27.5) * mm, "end": v(-25.48, 27.5) * mm});
            skLineSegment(sketch, "E167.MirrorCS", {"start": v(42.52, 27.5) * mm, "end": v(25.48, 27.5) * mm});
            skLineSegment(sketch, "E168.MirrorCS", {"start": v(31.17, 7) * mm, "end": v(25.48, 27.5) * mm});
            skLineSegment(sketch, "E169.MirrorCS", {"start": v(36.93, 7) * mm, "end": v(31.17, 7) * mm});
            skLineSegment(sketch, "E170.MirrorCS", {"start": v(42.52, 27.5) * mm, "end": v(36.93, 7) * mm});
            skLineSegment(sketch, "E171.MirrorCS", {"start": v(37.05, 6) * mm, "end": v(37.05, 3.5) * mm});
            skLineSegment(sketch, "E172.MirrorCS", {"start": v(37.05, 6) * mm, "end": v(31.05, 6) * mm});
            skLineSegment(sketch, "E173.MirrorCS", {"start": v(31.05, 6) * mm, "end": v(31.05, 3.5) * mm});
            skLineSegment(sketch, "E174.MirrorCS", {"start": v(37.05, 3.5) * mm, "end": v(31.05, 3.5) * mm});
            skSolve(sketch);
        }
        {
            var Q0;
            Q0 = qSketchRegion(id + "F4", true);
            var Q1;
            {var subQ0=sQuery(id+"F4.wireOp",EDGE,"oPhzmwcv-fS6T-XuVg-xpFZ-B5Fyl6x3LwKG");Q1=makeQuery(id+"F4.imprint","IMPRINT",FACE,{"disambiguationData":[TD([[makeQuery(id+"F4.imprint","IMPRINT",EDGE,{"derivedFrom":subQ0}),1.0]])]});}
            var Q2;
            {var subQ0=sQuery(id+"F4.wireOp",EDGE,"a919dabb-46be-4e27-a877-980e6d90d1850.MirrorCS");Q2=makeQuery(id+"F4.imprint","IMPRINT",FACE,{"disambiguationData":[TD([[makeQuery(id+"F4.imprint","IMPRINT",EDGE,{"derivedFrom":subQ0}),-1.0]])]});}
            extrude(context, id + "F5", {"entities" : qUnion([Q0, Q1, Q2]), "operationType" : NewBodyOperationType.REMOVE, "oppositeDirection" : true, "depth" : 100 * mm, "offsetDistance" : 25 * mm});
        }
        {
            var Q0;
            {var subQ0=sQuery(id+"F4.wireOp",EDGE,"oPhzmwcv-fS6T-XuVg-xpFZ-B5Fyl6x3LwKG");var subQ2=sQuery(id+"F2.wireOp",EDGE,"E154.right");Q0=makeQuery(id+"F5.boolean.opBoolean","COPY",EDGE,{"disambiguationData":[TD([makeQuery(id+"F1.opExtrude","SWEPT_FACE",FACE,{"disambiguationData":[OSD([sQuery(id+"F0.wireOp",EDGE,"E0.right")])]})])],"derivedFrom":makeQuery(id+"F5.opExtrude","SWEPT_EDGE",EDGE,{"disambiguationData":[OSD([subQ2,subQ0])]})});}
            var Q1;
            {var subQ1=sQuery(id+"F2.wireOp",EDGE,"E154.right");var subQ2=sQuery(id+"F4.wireOp",EDGE,"qnzgcZAI-1nWb-YeSE-jtA6-1WbSOZ8IEiMB");Q1=makeQuery(id+"F5.boolean.opBoolean","COPY",EDGE,{"disambiguationData":[TD([makeQuery(id+"F1.opExtrude","SWEPT_FACE",FACE,{"disambiguationData":[OSD([sQuery(id+"F0.wireOp",EDGE,"E0.right")])]})])],"derivedFrom":makeQuery(id+"F5.opExtrude","SWEPT_EDGE",EDGE,{"disambiguationData":[OSD([subQ1,subQ2])]})});}
            var Q2;
            {var subQ0=sQuery(id+"F4.wireOp",EDGE,"a919dabb-46be-4e27-a877-980e6d90d1850.MirrorCS");var subQ2=sQuery(id+"F2.wireOp",EDGE,"E154.right");Q2=makeQuery(id+"F5.boolean.opBoolean","COPY",EDGE,{"disambiguationData":[TD([makeQuery(id+"F1.opExtrude","SWEPT_FACE",FACE,{"disambiguationData":[OSD([sQuery(id+"F0.wireOp",EDGE,"E0.right")])]})])],"derivedFrom":makeQuery(id+"F5.opExtrude","SWEPT_EDGE",EDGE,{"disambiguationData":[OSD([subQ2,subQ0])]})});}
            var Q3;
            {var subQ1=sQuery(id+"F2.wireOp",EDGE,"E154.right");var subQ2=sQuery(id+"F4.wireOp",EDGE,"3f641d85-280b-4080-bc0a-306f409039ed0.MirrorCS");Q3=makeQuery(id+"F5.boolean.opBoolean","COPY",EDGE,{"disambiguationData":[TD([makeQuery(id+"F1.opExtrude","SWEPT_FACE",FACE,{"disambiguationData":[OSD([sQuery(id+"F0.wireOp",EDGE,"E0.right")])]})])],"derivedFrom":makeQuery(id+"F5.opExtrude","SWEPT_EDGE",EDGE,{"disambiguationData":[OSD([subQ1,subQ2])]})});}
            var Q4;
            {var subQ1=sQuery(id+"F2.wireOp",EDGE,"E154.right");var subQ3=sQuery(id+"F4.wireOp",EDGE,"3f641d85-280b-4080-bc0a-306f409039ed0.MirrorCS");Q4=makeQuery(id+"F5.boolean.opBoolean","COPY",EDGE,{"disambiguationData":[TD([makeQuery(id+"F1.opExtrude","SWEPT_FACE",FACE,{"disambiguationData":[OSD([sQuery(id+"F0.wireOp",EDGE,"E0.left")])]})])],"derivedFrom":makeQuery(id+"F5.opExtrude","SWEPT_EDGE",EDGE,{"disambiguationData":[OSD([subQ1,subQ3])]})});}
            var Q5;
            {var subQ0=sQuery(id+"F4.wireOp",EDGE,"a919dabb-46be-4e27-a877-980e6d90d1850.MirrorCS");var subQ2=sQuery(id+"F2.wireOp",EDGE,"E154.right");Q5=makeQuery(id+"F5.boolean.opBoolean","COPY",EDGE,{"disambiguationData":[TD([makeQuery(id+"F1.opExtrude","SWEPT_FACE",FACE,{"disambiguationData":[OSD([sQuery(id+"F0.wireOp",EDGE,"E0.left")])]})])],"derivedFrom":makeQuery(id+"F5.opExtrude","SWEPT_EDGE",EDGE,{"disambiguationData":[OSD([subQ2,subQ0])]})});}
            var Q6;
            {var subQ1=sQuery(id+"F2.wireOp",EDGE,"E154.right");var subQ3=sQuery(id+"F4.wireOp",EDGE,"qnzgcZAI-1nWb-YeSE-jtA6-1WbSOZ8IEiMB");Q6=makeQuery(id+"F5.boolean.opBoolean","COPY",EDGE,{"disambiguationData":[TD([makeQuery(id+"F1.opExtrude","SWEPT_FACE",FACE,{"disambiguationData":[OSD([sQuery(id+"F0.wireOp",EDGE,"E0.left")])]})])],"derivedFrom":makeQuery(id+"F5.opExtrude","SWEPT_EDGE",EDGE,{"disambiguationData":[OSD([subQ1,subQ3])]})});}
            var Q7;
            {var subQ0=sQuery(id+"F4.wireOp",EDGE,"oPhzmwcv-fS6T-XuVg-xpFZ-B5Fyl6x3LwKG");var subQ2=sQuery(id+"F2.wireOp",EDGE,"E154.right");Q7=makeQuery(id+"F5.boolean.opBoolean","COPY",EDGE,{"disambiguationData":[TD([makeQuery(id+"F1.opExtrude","SWEPT_FACE",FACE,{"disambiguationData":[OSD([sQuery(id+"F0.wireOp",EDGE,"E0.left")])]})])],"derivedFrom":makeQuery(id+"F5.opExtrude","SWEPT_EDGE",EDGE,{"disambiguationData":[OSD([subQ2,subQ0])]})});}
            fillet(context, id + "F6", {"entities" : qUnion([Q0, Q1, Q2, Q3, Q4, Q5, Q6, Q7]), "radius" : 2.5 * mm, "tangentPropagation" : true, "allowEdgeOverflow" : false});
        }
        {
            var Q0;
            Q0=makeQuery(id+"F3.boolean.opBoolean","MERGE",FACE,{"derivedFrom":[makeQuery(id+"F1.opExtrude","SWEPT_FACE",FACE,{"disambiguationData":[OSD([sQuery(id+"F0.wireOp",EDGE,"E117.5")])]}),makeQuery(id+"F3.opExtrude","SWEPT_FACE",FACE,{"disambiguationData":[OSD([sQuery(id+"F2.wireOp",EDGE,"E154.right")])]})]});
            var sketch = newSketch(context, id + "F7", { "sketchPlane" : qUnion([Q0])});
            skLineSegment(sketch, "E175.bottom", {"start": v(-31.05, 6) * mm, "end": v(-37.05, 6) * mm});
            skLineSegment(sketch, "E175.top", {"start": v(-31.05, 7.6) * mm, "end": v(-37.05, 7.6) * mm});
            skLineSegment(sketch, "E175.left", {"start": v(-31.05, 6) * mm, "end": v(-31.05, 7.6) * mm});
            skLineSegment(sketch, "E175.right", {"start": v(-37.05, 6) * mm, "end": v(-37.05, 7.6) * mm});
            skSolve(sketch);
        }
        {
            var Q0;
            Q0 = qSketchRegion(id + "F7", true);
            extrude(context, id + "F8", {"entities" : qUnion([Q0]), "operationType" : NewBodyOperationType.REMOVE, "oppositeDirection" : true, "depth" : 1.5 * mm, "offsetDistance" : 25 * mm});
        }
        {
            var Q0;
            Q0=makeQuery(id+"F3.boolean.opBoolean","MERGE",FACE,{"derivedFrom":[makeQuery(id+"F1.opExtrude","SWEPT_FACE",FACE,{"disambiguationData":[OSD([sQuery(id+"F0.wireOp",EDGE,"E117.5")])]}),makeQuery(id+"F3.opExtrude","SWEPT_FACE",FACE,{"disambiguationData":[OSD([sQuery(id+"F2.wireOp",EDGE,"E154.right")])]})]});
            var sketch = newSketch(context, id + "F9", { "sketchPlane" : qUnion([Q0])});
            skLineSegment(sketch, "E176.bottom", {"start": v(31.05, 6) * mm, "end": v(37.05, 6) * mm});
            skLineSegment(sketch, "E176.top", {"start": v(31.05, 7.6) * mm, "end": v(37.05, 7.6) * mm});
            skLineSegment(sketch, "E176.left", {"start": v(31.05, 6) * mm, "end": v(31.05, 7.6) * mm});
            skLineSegment(sketch, "E176.right", {"start": v(37.05, 6) * mm, "end": v(37.05, 7.6) * mm});
            skSolve(sketch);
        }
        {
            var Q0;
            Q0 = qSketchRegion(id + "F9", true);
            extrude(context, id + "F10", {"entities" : qUnion([Q0]), "operationType" : NewBodyOperationType.REMOVE, "oppositeDirection" : true, "depth" : 1.5 * mm, "offsetDistance" : 25 * mm});
        }
        {
            var Q0;
            Q0=makeQuery(id+"F3.boolean.opBoolean","MERGE",FACE,{"derivedFrom":[makeQuery(id+"F1.opExtrude","SWEPT_FACE",FACE,{"disambiguationData":[OSD([sQuery(id+"F0.wireOp",EDGE,"E117.1")])]}),makeQuery(id+"F3.opExtrude","SWEPT_FACE",FACE,{"disambiguationData":[OSD([sQuery(id+"F2.wireOp",EDGE,"E154.left")])]})]});
            var sketch = newSketch(context, id + "F11", { "sketchPlane" : qUnion([Q0])});
            skLineSegment(sketch, "E177.bottom", {"start": v(-37.05, 6) * mm, "end": v(-31.05, 6) * mm});
            skLineSegment(sketch, "E177.top", {"start": v(-37.05, 7.6) * mm, "end": v(-31.05, 7.6) * mm});
            skLineSegment(sketch, "E177.left", {"start": v(-37.05, 6) * mm, "end": v(-37.05, 7.6) * mm});
            skLineSegment(sketch, "E177.right", {"start": v(-31.05, 6) * mm, "end": v(-31.05, 7.6) * mm});
            skLineSegment(sketch, "E178.bottom", {"start": v(31.05, 6) * mm, "end": v(37.05, 6) * mm});
            skLineSegment(sketch, "E178.top", {"start": v(31.05, 7.6) * mm, "end": v(37.05, 7.6) * mm});
            skLineSegment(sketch, "E178.left", {"start": v(31.05, 6) * mm, "end": v(31.05, 7.6) * mm});
            skLineSegment(sketch, "E178.right", {"start": v(37.05, 6) * mm, "end": v(37.05, 7.6) * mm});
            skSolve(sketch);
        }
        {
            var Q0;
            Q0 = qSketchRegion(id + "F11", true);
            extrude(context, id + "F12", {"entities" : qUnion([Q0]), "operationType" : NewBodyOperationType.REMOVE, "oppositeDirection" : true, "depth" : 1.5 * mm, "offsetDistance" : 25 * mm});
        }
    });
